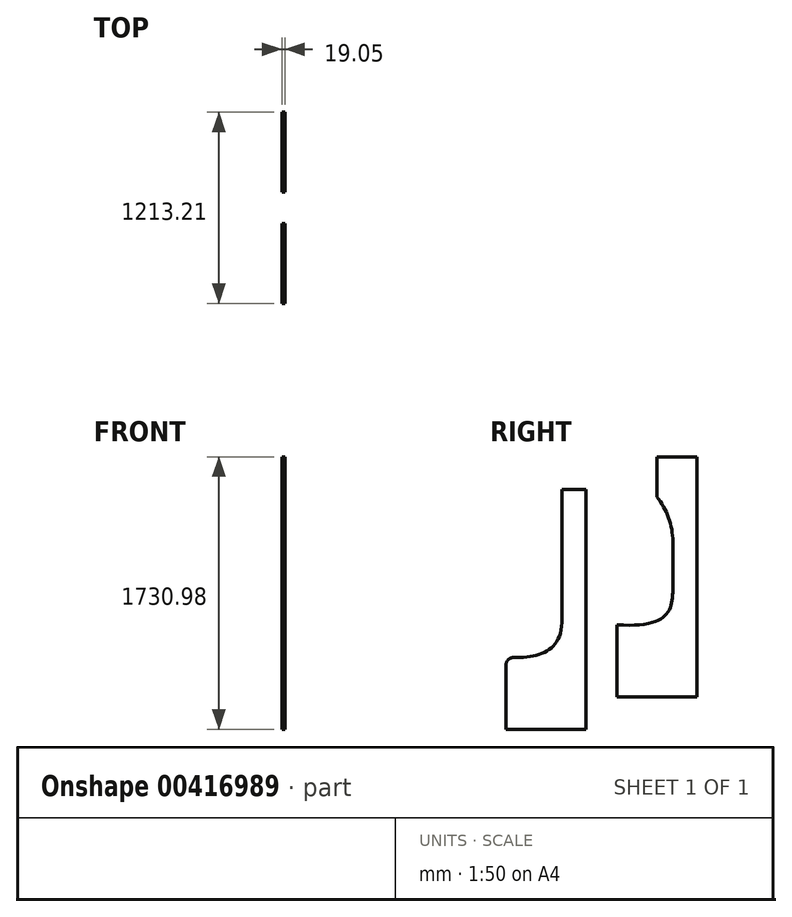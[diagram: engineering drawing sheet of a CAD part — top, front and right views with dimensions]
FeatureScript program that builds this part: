
annotation { "Feature Type Name" : "Feature", "Feature Type Description" : "" }
export const myFeature = defineFeature(function(context is Context, id is Id, definition is map)
    precondition{}
    {
        {
            var Q0;
            Q0=qCreatedBy(makeId("Right.planeOp"),FACE);
            var sketch = newSketch(context, id + "F0", { "sketchPlane" : qUnion([Q0])});
            skLineSegment(sketch, "E0", {"start": v(254, 925.8) * mm, "end": v(254, -598.2) * mm});
            skLineSegment(sketch, "E1", {"start": v(254, -598.2) * mm, "end": v(-254, -598.2) * mm});
            skLineSegment(sketch, "E2", {"start": v(-253.56, -598.2) * mm, "end": v(-253.56, -141) * mm});
            skLineSegment(sketch, "E3", {"start": v(254, 925.8) * mm, "end": v(0, 925.8) * mm});
            skLineSegment(sketch, "E4", {"start": v(0, 925.8) * mm, "end": v(0, 671.8) * mm});
            skPoint(sketch, "E5", {"position": v(254, 163.8) * mm});
            skLineSegment(sketch, "E6", {"start": v(101.6, 82.06) * mm, "end": v(101.6, 386.86) * mm});
            skArc(sketch, "E7", {"start": v(101.6, 386.86) * mm, "mid": v(75.44, 538.12) * mm, "end": v(0, 671.8) * mm});
            skFitSpline(sketch, "E8", {"points": [v(101.6, 82.06) * mm, v(-253.56, -141) * mm], "startDerivative": vector(-5.67, -407.64) * mm, "endDerivative": vector(-980.27, 66.54) * mm});
            skSolve(sketch);
        }
        {
            var Q0;
            Q0 = qSketchRegion(id + "F0", true);
            extrude(context, id + "F1", {"entities" : qUnion([Q0]), "depth" : 19.05 * mm});
        }
        {
            var Q0;
            Q0=qCreatedBy(makeId("Right.planeOp"),FACE);
            var sketch = newSketch(context, id + "F2", { "sketchPlane" : qUnion([Q0])});
            skLineSegment(sketch, "E9", {"start": v(-451.21, 718.83) * mm, "end": v(-451.21, -805.17) * mm});
            skLineSegment(sketch, "E10", {"start": v(-451.21, 718.83) * mm, "end": v(-603.61, 718.83) * mm});
            skLineSegment(sketch, "E11", {"start": v(-451.21, -805.17) * mm, "end": v(-959.21, -805.17) * mm});
            skLineSegment(sketch, "E12", {"start": v(-959.21, -805.17) * mm, "end": v(-959.21, -400.04) * mm});
            skLineSegment(sketch, "E13", {"start": v(-603.61, 718.83) * mm, "end": v(-603.61, -100.81) * mm});
            skFitSpline(sketch, "E14", {"points": [v(-603.61, -100.81) * mm, v(-959.21, -347.97) * mm], "startDerivative": vector(26.6, -695.8) * mm, "endDerivative": vector(-546.7, 23.91) * mm});
            skArc(sketch, "E15.filletArc", {"start": v(-908.25, -349.24) * mm, "mid": v(-944.27, -364.06) * mm, "end": v(-959.21, -400.04) * mm});
            skSolve(sketch);
        }
        {
            var Q0;
            Q0=makeQuery(id+"F2.imprint","IMPRINT",FACE,{"disambiguationData":[TD([[makeQuery(id+"F2.imprint","IMPRINT",EDGE,{"derivedFrom":sQuery(id+"F2.wireOp",EDGE,"E9")}),-1.0]])]});
            extrude(context, id + "F3", {"entities" : qUnion([Q0]), "depth" : 19.05 * mm});
        }
    });
